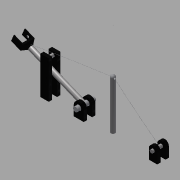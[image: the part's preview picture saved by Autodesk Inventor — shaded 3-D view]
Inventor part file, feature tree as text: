
AUTODESK INVENTOR PART (.ipt)
format: ipt  version: 2015 (Build 190159000, 159)  size: 310,272 bytes
history: native  units: in
note: dims shown in document units (in); Inventor stores cm internally (conversion verified against a paired STEP export)
features: sketch x17, extrude x13, plane x8, mirror x3, sweep x2, other x2, loft x1, thread x1, fillet x1
ambient origin geometry x8: Origin, YZ Plane, XZ Plane, XY Plane, X Axis, Y Axis, Z Axis, Center Point
bodies: Solid1 (feature_tree)
feature tree (48):
  extrude  "Extrusion1"  Depth=0.2362in
  plane  "Work Plane1"
  mirror  "Mirror1"
  plane  "Work Plane2"
  extrude  "Extrusion2"  Depth=0.1181in
  plane  "Work Plane8"
  extrude  "Extrusion3"  Depth=0.0591in
  plane  "Work Plane5"
  extrude  "Extrusion4"  Depth=0.1102in
  loft  "Loft1"
  extrude  "Extrusion5"  Depth=0.0787in
  extrude  "Extrusion6"  Depth=0.0394in
  thread  "Thread1"  [1 undecoded]
  extrude  "Extrusion7"  TaperAngle=0.0deg  [1 undecoded]
  mirror  "Mirror2"
  extrude  "Extrusion8"  Depth=0.0197in
  plane  "Work Plane9"
  extrude  "Extrusion9"  Depth=0.0591in
  plane  "Work Plane10"
  extrude  "Extrusion10"  Depth=0.3937in TaperAngle=0.0deg
  fillet  "Fillet1"  Radius=0.1969in
  extrude  "Extrusion11"  Depth=0.0787in
  mirror  "Mirror3"
  extrude  "Extrusion12"  Depth=0.0984in
  sketch  "Sketch21"  dims[d41=0.2756in d42=0.0in d45=0.0984in]
  plane  "Work Plane11"
  sweep  "Sweep1"
  extrude  "Extrusion13"  Depth=0.0591in
  sketch  "Sketch24"  dims[d51=0.3937in d52=0.0in d53=0.0492in]
  plane  "Work Plane12"
  sweep  "Sweep2"
  sketch  "Sketch1"  dims[d0=0.5906in d1=0.2362in]
  sketch  "Sketch2"  dims[d2=0.2362in d3=0.1181in]
  sketch  "Sketch6"  dims[d4=0.0787in d5=0.0in d6=0.0591in]
  sketch  "Sketch8"  dims[d7=0.0787in d8=0.1102in]
  other  "Edges1"
  other  "Edges2"
  sketch  "Sketch9"  dims[d9=0.4331in d10=0.0in d13=0.1102in]
  sketch  "Sketch10"  dims[d14=1.378in d15=0.0in d18=0.0787in]
  sketch  "Sketch13"  dims[d19=0.2756in d20=0.1575in d21=0.0394in d22=0.0in]
  sketch  "Sketch14"  dims[d23=0.0in d24=90.0deg d25=0.0in d26=90.0deg]
  sketch  "Sketch17"  dims[d27=0.0197in d28=0.0197in]
  sketch  "Sketch18"  dims[d29=0.1969in d30=0.0in d31=0.0591in]
  sketch  "Sketch19"  dims[d32=0.1969in d33=0.0in d34=0.3937in d35=0.0in d37=0.1969in]
  sketch  "Sketch20"  dims[d38=0.0787in d39=0.0in d40=0.0787in]
  sketch  "Sketch22"  dims[d46=1.1811in d47=0.0in d48=0.7874in]
  sketch  "Sketch23"  dims[d49=0.0591in d50=0.0472in]
  sketch  "Sketch25"  dims[d54=1.7717in d55=0.3543in d56=0.1969in d57=0.2362in d58=0.1969in d59=0.0787in d60=0.0in d61=0.0787in d62=0.315in d63=0.0394in d64=0.0in d65=0.0in d66=0.0039in d67=0.0in d68=0.0in d69=0.0394in d70=0.0in d71=0.0039in d72=0.0in d73=0.0in]
note: 2 required parameter values undecoded (feature->parameter linkage not recoverable at this tier; creation-order binding heuristic only, values carry confidence <= 0.55)
